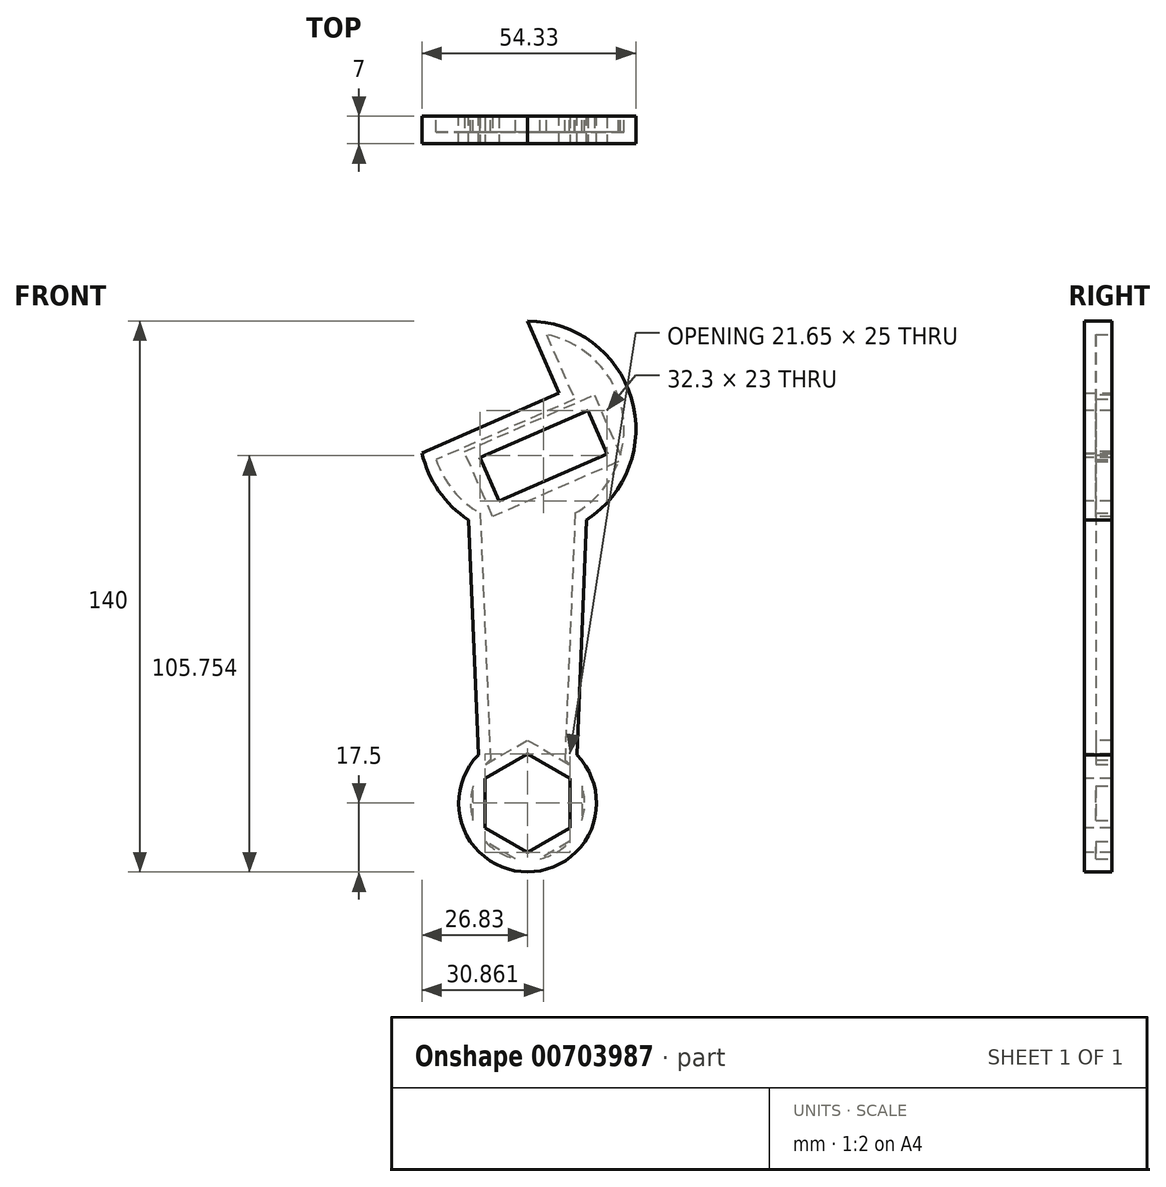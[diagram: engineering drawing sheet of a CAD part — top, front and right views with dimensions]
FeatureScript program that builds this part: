
annotation { "Feature Type Name" : "Feature", "Feature Type Description" : "" }
export const myFeature = defineFeature(function(context is Context, id is Id, definition is map)
    precondition{}
    {
        {
            var Q0;
            Q0=qCreatedBy(makeId("Front.planeOp"),FACE);
            var sketch = newSketch(context, id + "F0", { "sketchPlane" : qUnion([Q0])});
            skArc(sketch, "E0", {"start": v(-12.5, 29.75) * mm, "mid": v(0, 0) * mm, "end": v(12.5, 29.75) * mm});
            skArc(sketch, "E1", {"start": v(-26.83, 106.47) * mm, "mid": v(-22.58, 96.8) * mm, "end": v(-15, 89.45) * mm});
            skLineSegment(sketch, "E2", {"start": v(-15, 89.45) * mm, "end": v(-12.5, 29.75) * mm});
            skLineSegment(sketch, "E3", {"start": v(15, 89.45) * mm, "end": v(12.5, 29.75) * mm});
            skLineSegment(sketch, "E4", {"start": v(0, 140) * mm, "end": v(8, 121.67) * mm});
            skLineSegment(sketch, "E5", {"start": v(8, 121.67) * mm, "end": v(-26.83, 106.47) * mm});
            skArc(sketch, "E6.trimOffspring", {"start": v(15, 89.45) * mm, "mid": v(26.36, 120.32) * mm, "end": v(0, 140) * mm});
            skSolve(sketch);
        }
        {
            var Q0;
            Q0=makeQuery(id+"F0.imprint","IMPRINT",FACE,{"disambiguationData":[TD([[makeQuery(id+"F0.imprint","IMPRINT",EDGE,{"derivedFrom":sQuery(id+"F0.wireOp",EDGE,"E0")}),1.0]])]});
            extrude(context, id + "F1", {"entities" : qUnion([Q0]), "depth" : 7 * mm, "offsetDistance" : 25 * mm});
        }
        {
            var Q0;
            Q0=makeQuery(id+"F1.opExtrude","CAP_FACE",FACE,{"disambiguationData":[OSD([sQuery(id+"F0.wireOp",EDGE,"E0"),sQuery(id+"F0.wireOp",EDGE,"E1"),sQuery(id+"F0.wireOp",EDGE,"E2"),sQuery(id+"F0.wireOp",EDGE,"E3"),sQuery(id+"F0.wireOp",EDGE,"E4"),sQuery(id+"F0.wireOp",EDGE,"E5"),sQuery(id+"F0.wireOp",EDGE,"E6.trimOffspring")])],"isStart":false});
            var sketch = newSketch(context, id + "F2", { "sketchPlane" : qUnion([Q0])});
            skCircle(sketch, "E7.cCircle", {"center": v(0, 17.5) * mm, "radius": 12.5 * mm, "construction": true});
            skLineSegment(sketch, "E7.0", {"start": v(0, 30) * mm, "end": v(10.83, 23.75) * mm});
            skLineSegment(sketch, "E7.1", {"start": v(10.83, 23.75) * mm, "end": v(10.83, 11.25) * mm});
            skLineSegment(sketch, "E7.2", {"start": v(10.83, 11.25) * mm, "end": v(0, 5) * mm});
            skLineSegment(sketch, "E7.3", {"start": v(0, 5) * mm, "end": v(-10.83, 11.25) * mm});
            skLineSegment(sketch, "E7.4", {"start": v(-10.83, 11.25) * mm, "end": v(-10.83, 23.75) * mm});
            skLineSegment(sketch, "E7.5", {"start": v(-10.83, 23.75) * mm, "end": v(0, 30) * mm});
            skSolve(sketch);
        }
        {
            var Q0;
            Q0=makeQuery(id+"F2.imprint","IMPRINT",FACE,{"disambiguationData":[TD([[makeQuery(id+"F2.imprint","IMPRINT",EDGE,{"derivedFrom":sQuery(id+"F2.wireOp",EDGE,"E7.0")}),-1.0]])]});
            extrude(context, id + "F3", {"entities" : qUnion([Q0]), "operationType" : NewBodyOperationType.REMOVE, "oppositeDirection" : true, "depth" : 25 * mm, "offsetDistance" : 25 * mm});
        }
        {
            var Q0;
            Q0=makeQuery(id+"F1.opExtrude","CAP_FACE",FACE,{"disambiguationData":[OSD([sQuery(id+"F0.wireOp",EDGE,"E0"),sQuery(id+"F0.wireOp",EDGE,"E1"),sQuery(id+"F0.wireOp",EDGE,"E2"),sQuery(id+"F0.wireOp",EDGE,"E3"),sQuery(id+"F0.wireOp",EDGE,"E4"),sQuery(id+"F0.wireOp",EDGE,"E5"),sQuery(id+"F0.wireOp",EDGE,"E6.trimOffspring")])],"isStart":false});
            var sketch = newSketch(context, id + "F4", { "sketchPlane" : qUnion([Q0])});
            skLineSegment(sketch, "E8", {"start": v(-12.12, 105.26) * mm, "end": v(15.38, 117.25) * mm});
            skLineSegment(sketch, "E9", {"start": v(15.38, 117.25) * mm, "end": v(20.18, 106.25) * mm});
            skLineSegment(sketch, "E10", {"start": v(20.18, 106.25) * mm, "end": v(-7.32, 94.26) * mm});
            skLineSegment(sketch, "E11", {"start": v(-7.32, 94.26) * mm, "end": v(-12.12, 105.26) * mm});
            skSolve(sketch);
        }
        {
            var Q0;
            Q0=makeQuery(id+"F4.imprint","IMPRINT",FACE,{"disambiguationData":[TD([[makeQuery(id+"F4.imprint","IMPRINT",EDGE,{"derivedFrom":sQuery(id+"F4.wireOp",EDGE,"E8")}),-1.0]])]});
            extrude(context, id + "F5", {"entities" : qUnion([Q0]), "operationType" : NewBodyOperationType.REMOVE, "oppositeDirection" : true, "depth" : 25 * mm, "offsetDistance" : 25 * mm});
        }
        {
            var Q0;
            Q0=makeQuery(id+"F1.opExtrude","CAP_FACE",FACE,{"disambiguationData":[OSD([sQuery(id+"F0.wireOp",EDGE,"E0"),sQuery(id+"F0.wireOp",EDGE,"E1"),sQuery(id+"F0.wireOp",EDGE,"E2"),sQuery(id+"F0.wireOp",EDGE,"E3"),sQuery(id+"F0.wireOp",EDGE,"E4"),sQuery(id+"F0.wireOp",EDGE,"E5"),sQuery(id+"F0.wireOp",EDGE,"E6.trimOffspring")])],"isStart":true});
            shell(context, id + "F6", {"entities" : qUnion([Q0]), "thickness" : 3 * mm});
        }
    });
